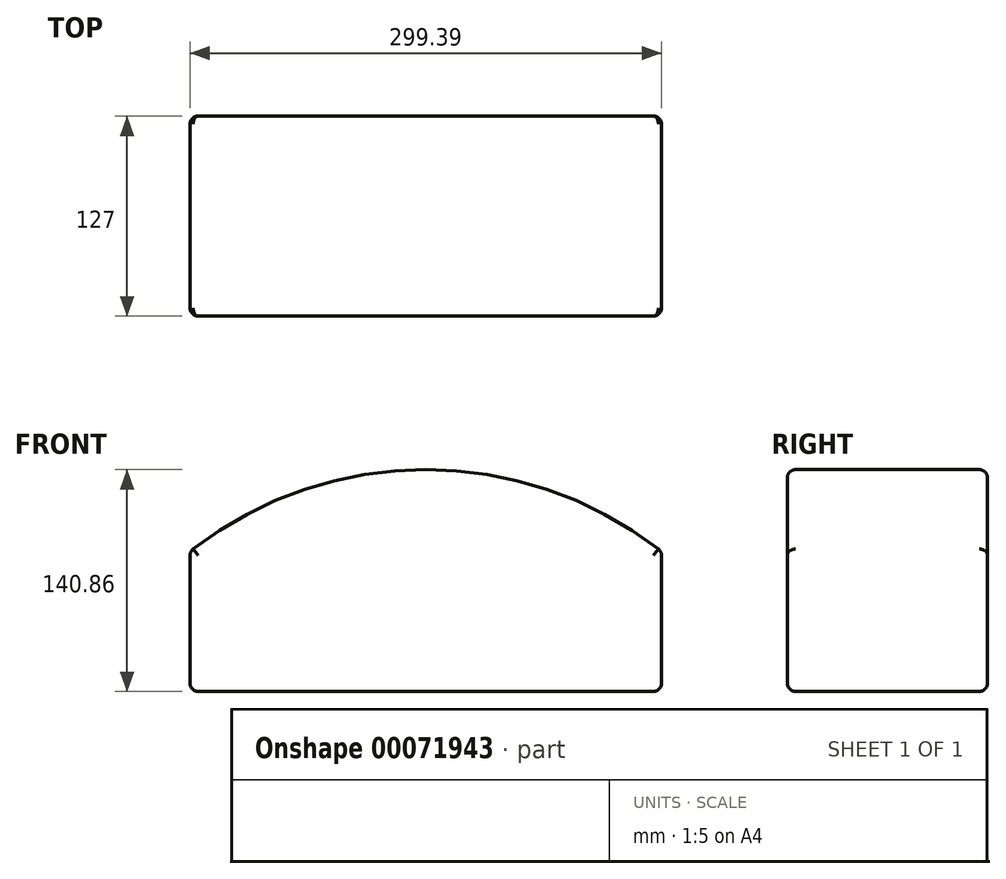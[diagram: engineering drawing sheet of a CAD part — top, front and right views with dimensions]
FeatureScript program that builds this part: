
annotation { "Feature Type Name" : "Feature", "Feature Type Description" : "" }
export const myFeature = defineFeature(function(context is Context, id is Id, definition is map)
    precondition{}
    {
        {
            var Q0;
            Q0=qCreatedBy(makeId("Front.planeOp"),FACE);
            var sketch = newSketch(context, id + "F0", { "sketchPlane" : qUnion([Q0])});
            skLineSegment(sketch, "E0", {"start": v(-143.9, 0) * mm, "end": v(-143.9, 88.88) * mm});
            skLineSegment(sketch, "E1", {"start": v(155.49, 0) * mm, "end": v(-143.9, 0) * mm});
            skLineSegment(sketch, "E2", {"start": v(155.49, 88.88) * mm, "end": v(155.49, 0) * mm});
            skArc(sketch, "E3", {"start": v(155.49, 88.88) * mm, "mid": v(5.8, 140.86) * mm, "end": v(-143.9, 88.88) * mm});
            skSolve(sketch);
        }
        {
            var Q0;
            Q0 = qSketchRegion(id + "F0", true);
            extrude(context, id + "F1", {"entities" : qUnion([Q0]), "depth" : 127 * mm});
        }
        {
            var Q0;
            Q0=makeQuery(id+"F1.opExtrude","SWEPT_FACE",FACE,{"disambiguationData":[OSD([sQuery(id+"F0.wireOp",EDGE,"E0")])]});
            fillet(context, id + "F2", {"entities" : qUnion([Q0]), "radius" : 5.08 * mm, "tangentPropagation" : true, "allowEdgeOverflow" : false});
        }
        {
            var Q0;
            Q0=makeQuery(id+"F1.opExtrude","SWEPT_FACE",FACE,{"disambiguationData":[OSD([sQuery(id+"F0.wireOp",EDGE,"E1")])]});
            var Q1;
            Q1=makeQuery(id+"F1.opExtrude","SWEPT_FACE",FACE,{"disambiguationData":[OSD([sQuery(id+"F0.wireOp",EDGE,"E2")])]});
            fillet(context, id + "F3", {"entities" : qUnion([Q0, Q1]), "radius" : 5.08 * mm, "tangentPropagation" : true, "allowEdgeOverflow" : false});
        }
        {
            var Q0;
            Q0=makeQuery(id+"F1.opExtrude","CAP_FACE",FACE,{"disambiguationData":[OSD([sQuery(id+"F0.wireOp",EDGE,"E0"),sQuery(id+"F0.wireOp",EDGE,"E1"),sQuery(id+"F0.wireOp",EDGE,"E2"),sQuery(id+"F0.wireOp",EDGE,"E3")])],"isStart":true});
            var Q1;
            Q1=makeQuery(id+"F1.opExtrude","CAP_FACE",FACE,{"disambiguationData":[OSD([sQuery(id+"F0.wireOp",EDGE,"E0"),sQuery(id+"F0.wireOp",EDGE,"E1"),sQuery(id+"F0.wireOp",EDGE,"E2"),sQuery(id+"F0.wireOp",EDGE,"E3")])],"isStart":false});
            var Q2;
            Q2=makeQuery(id+"F1.opExtrude","SWEPT_FACE",FACE,{"disambiguationData":[OSD([sQuery(id+"F0.wireOp",EDGE,"E3")])]});
            var Q3;
            Q3=makeQuery(id+"F1.opExtrude","SWEPT_FACE",FACE,{"disambiguationData":[OSD([sQuery(id+"F0.wireOp",EDGE,"E1")])]});
            fillet(context, id + "F4", {"entities" : qUnion([Q0, Q1, Q2, Q3]), "radius" : 5.08 * mm, "tangentPropagation" : true, "allowEdgeOverflow" : false});
        }
    });
